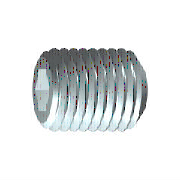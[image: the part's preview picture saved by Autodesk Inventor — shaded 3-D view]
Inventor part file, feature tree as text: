
AUTODESK INVENTOR PART (.ipt)
format: ipt  version: 2011 (Build 150239000, 239)  size: 153,600 bytes
history: native  units: mm (DEFAULTED — no unit token found)
features: extrude x1, other x1, plane x1
ambient origin geometry x8: Origin, YZ Plane, XZ Plane, XY Plane, X Axis, Y Axis, Z Axis, Center Point
bodies: Solid1 (feature_tree), Body (feature_tree)
feature tree (3):
  extrude  "Slot"  Depth=3.175mm
  other  "Work Axis1"
  plane  "Work Plane1"
